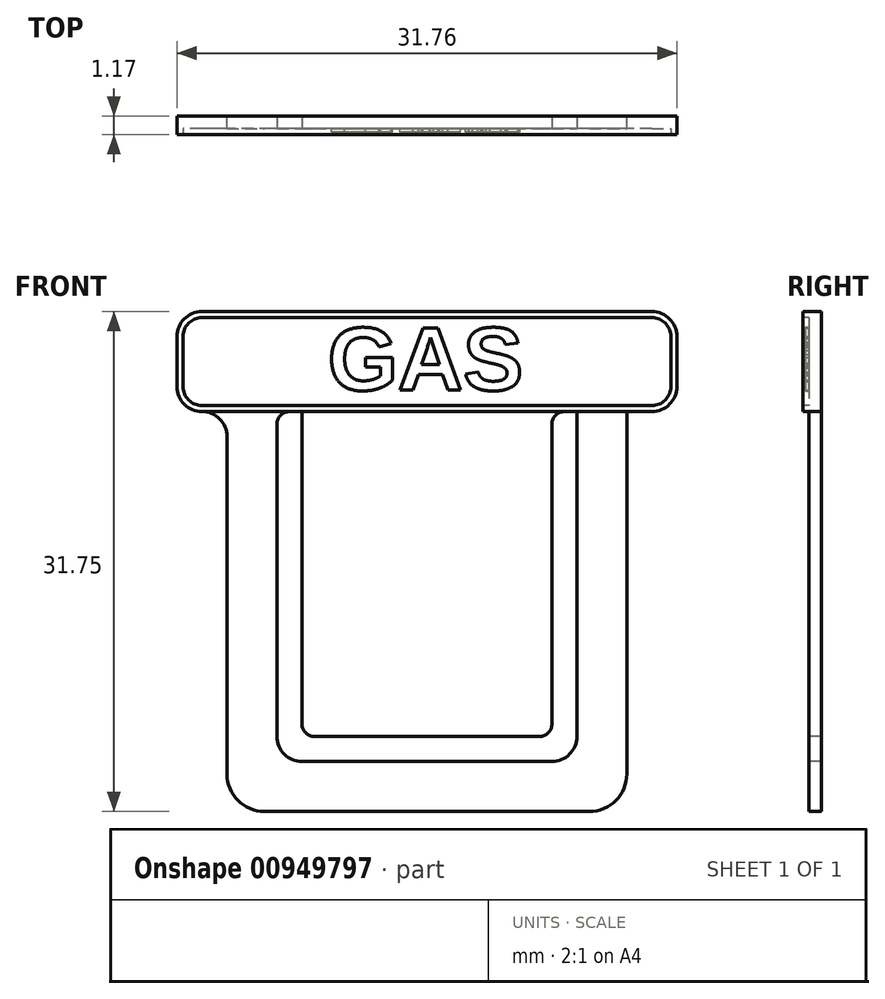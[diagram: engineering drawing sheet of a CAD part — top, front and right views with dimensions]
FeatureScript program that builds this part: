
annotation { "Feature Type Name" : "Feature", "Feature Type Description" : "" }
export const myFeature = defineFeature(function(context is Context, id is Id, definition is map)
    precondition{}
    {
        {
            var Q0;
            Q0=qCreatedBy(makeId("Front.planeOp"),FACE);
            var sketch = newSketch(context, id + "F0", { "sketchPlane" : qUnion([Q0])});
            skLineSegment(sketch, "E0.bottom", {"start": v(12.7, 12.7) * mm, "end": v(-12.7, 12.7) * mm});
            skLineSegment(sketch, "E0.top", {"start": v(12.7, -12.7) * mm, "end": v(-12.7, -12.7) * mm});
            skLineSegment(sketch, "E0.left", {"start": v(12.7, 12.7) * mm, "end": v(12.7, -12.7) * mm});
            skLineSegment(sketch, "E0.right", {"start": v(-12.7, 12.7) * mm, "end": v(-12.7, -12.7) * mm});
            skPoint(sketch, "E0.middle", {"position": v(0, 0) * mm});
            skSolve(sketch);
        }
        {
            var Q0;
            Q0=makeQuery(id+"F0.imprint","IMPRINT",FACE,{"disambiguationData":[TD([[makeQuery(id+"F0.imprint","IMPRINT",EDGE,{"derivedFrom":sQuery(id+"F0.wireOp",EDGE,"E0.bottom")}),1.0]])]});
            extrude(context, id + "F1", {"entities" : qUnion([Q0]), "depth" : 0.8 * mm, "offsetDistance" : 25.4 * mm});
        }
        {
            var Q0;
            Q0=makeQuery(id+"F1.opExtrude","SWEPT_EDGE",EDGE,{"disambiguationData":[OSD([sQuery(id+"F0.wireOp",EDGE,"E0.top"),sQuery(id+"F0.wireOp",EDGE,"E0.left")])]});
            var Q1;
            Q1=makeQuery(id+"F1.opExtrude","SWEPT_EDGE",EDGE,{"disambiguationData":[OSD([sQuery(id+"F0.wireOp",EDGE,"E0.top"),sQuery(id+"F0.wireOp",EDGE,"E0.right")])]});
            fillet(context, id + "F2", {"entities" : qUnion([Q0, Q1]), "radius" : 2.38 * mm, "tangentPropagation" : true, "allowEdgeOverflow" : false});
        }
        {
            var Q0;
            Q0=makeQuery(id+"F1.opExtrude","CAP_FACE",FACE,{"disambiguationData":[OSD([sQuery(id+"F0.wireOp",EDGE,"E0.bottom"),sQuery(id+"F0.wireOp",EDGE,"E0.top"),sQuery(id+"F0.wireOp",EDGE,"E0.left"),sQuery(id+"F0.wireOp",EDGE,"E0.right")])],"isStart":false});
            var sketch = newSketch(context, id + "F3", { "sketchPlane" : qUnion([Q0])});
            skLineSegment(sketch, "E1.bottom", {"start": v(9.52, 12.7) * mm, "end": v(-9.53, 12.7) * mm});
            skLineSegment(sketch, "E1.top", {"start": v(9.53, -9.53) * mm, "end": v(-9.52, -9.53) * mm});
            skLineSegment(sketch, "E1.left", {"start": v(9.52, 12.7) * mm, "end": v(9.53, -9.53) * mm});
            skLineSegment(sketch, "E1.right", {"start": v(-9.53, 12.7) * mm, "end": v(-9.52, -9.53) * mm});
            skPoint(sketch, "E1.middle", {"position": v(0, 0) * mm});
            skSolve(sketch);
        }
        {
            var Q0;
            Q0=makeQuery(id+"F3.imprint","IMPRINT",FACE,{"disambiguationData":[TD([[makeQuery(id+"F3.imprint","IMPRINT",EDGE,{"derivedFrom":sQuery(id+"F3.wireOp",EDGE,"E1.bottom")}),1.0]])]});
            extrude(context, id + "F4", {"entities" : qUnion([Q0]), "operationType" : NewBodyOperationType.REMOVE, "oppositeDirection" : true, "depth" : 4.93 * mm, "offsetDistance" : 25.4 * mm});
        }
        {
            var Q0;
            Q0=makeQuery(id+"F1.opExtrude","CAP_FACE",FACE,{"disambiguationData":[OSD([sQuery(id+"F0.wireOp",EDGE,"E0.bottom"),sQuery(id+"F0.wireOp",EDGE,"E0.top"),sQuery(id+"F0.wireOp",EDGE,"E0.left"),sQuery(id+"F0.wireOp",EDGE,"E0.right")])],"isStart":false});
            var sketch = newSketch(context, id + "F5", { "sketchPlane" : qUnion([Q0])});
            skLineSegment(sketch, "E2.bottom", {"start": v(-15.88, 12.7) * mm, "end": v(15.88, 12.7) * mm});
            skLineSegment(sketch, "E2.top", {"start": v(-15.88, 19.05) * mm, "end": v(15.88, 19.05) * mm});
            skLineSegment(sketch, "E2.left", {"start": v(-15.88, 12.7) * mm, "end": v(-15.88, 19.05) * mm});
            skLineSegment(sketch, "E2.right", {"start": v(15.87, 12.7) * mm, "end": v(15.87, 19.05) * mm});
            skSolve(sketch);
        }
        {
            var Q0;
            Q0=makeQuery(id+"F5.imprint","IMPRINT",FACE,{"disambiguationData":[TD([[makeQuery(id+"F5.imprint","IMPRINT",EDGE,{"derivedFrom":sQuery(id+"F5.wireOp",EDGE,"E2.top")}),-1.0]])]});
            extrude(context, id + "F6", {"entities" : qUnion([Q0]), "operationType" : NewBodyOperationType.ADD, "oppositeDirection" : true, "depth" : 0.8 * mm, "offsetDistance" : 25.4 * mm});
        }
        {
            var Q0;
            Q0=makeQuery(id+"F6.opExtrude","SWEPT_EDGE",EDGE,{"disambiguationData":[OSD([sQuery(id+"F5.wireOp",EDGE,"E2.top"),sQuery(id+"F5.wireOp",EDGE,"E2.left")])]});
            var Q1;
            Q1=makeQuery(id+"F6.opExtrude","SWEPT_EDGE",EDGE,{"disambiguationData":[OSD([sQuery(id+"F5.wireOp",EDGE,"E2.top"),sQuery(id+"F5.wireOp",EDGE,"E2.right")])]});
            var Q2;
            Q2=makeQuery(id+"F6.opExtrude","SWEPT_EDGE",EDGE,{"disambiguationData":[OSD([sQuery(id+"F5.wireOp",EDGE,"E2.bottom"),sQuery(id+"F5.wireOp",EDGE,"E2.right")])]});
            var Q3;
            Q3=makeQuery(id+"F1.opExtrude","SWEPT_EDGE",EDGE,{"disambiguationData":[OSD([sQuery(id+"F0.wireOp",EDGE,"E0.bottom"),sQuery(id+"F0.wireOp",EDGE,"E0.left")])]});
            var Q4;
            Q4=makeQuery(id+"F6.opExtrude","SWEPT_EDGE",EDGE,{"disambiguationData":[OSD([sQuery(id+"F5.wireOp",EDGE,"E2.bottom"),sQuery(id+"F5.wireOp",EDGE,"E2.left")])]});
            var Q5;
            Q5=makeQuery(id+"F1.opExtrude","SWEPT_EDGE",EDGE,{"disambiguationData":[OSD([sQuery(id+"F0.wireOp",EDGE,"E0.bottom"),sQuery(id+"F0.wireOp",EDGE,"E0.right")])]});
            fillet(context, id + "F7", {"entities" : qUnion([Q0, Q1, Q2, Q3, Q4, Q5]), "radius" : 1.59 * mm, "tangentPropagation" : true, "allowEdgeOverflow" : false});
        }
        {
            var Q0;
            Q0=makeQuery(id+"F4.boolean.opBoolean","COPY",EDGE,{"derivedFrom":makeQuery(id+"F4.opExtrude","SWEPT_EDGE",EDGE,{"disambiguationData":[OSD([sQuery(id+"F3.wireOp",EDGE,"E1.top"),sQuery(id+"F3.wireOp",EDGE,"E1.right")])]})});
            var Q1;
            Q1=makeQuery(id+"F4.boolean.opBoolean","COPY",EDGE,{"derivedFrom":makeQuery(id+"F4.opExtrude","SWEPT_EDGE",EDGE,{"disambiguationData":[OSD([sQuery(id+"F3.wireOp",EDGE,"E1.top"),sQuery(id+"F3.wireOp",EDGE,"E1.left")])]})});
            fillet(context, id + "F8", {"entities" : qUnion([Q0, Q1]), "radius" : 1.59 * mm, "tangentPropagation" : true, "allowEdgeOverflow" : false});
        }
        {
            var Q0;
            Q0=makeQuery(id+"F6.boolean.opBoolean","MERGE",FACE,{"derivedFrom":[makeQuery(id+"F1.opExtrude","CAP_FACE",FACE,{"disambiguationData":[OSD([sQuery(id+"F0.wireOp",EDGE,"E0.bottom"),sQuery(id+"F0.wireOp",EDGE,"E0.top"),sQuery(id+"F0.wireOp",EDGE,"E0.left"),sQuery(id+"F0.wireOp",EDGE,"E0.right")])],"isStart":false}),makeQuery(id+"F6.opExtrude","CAP_FACE",FACE,{"disambiguationData":[OSD([sQuery(id+"F5.wireOp",EDGE,"E2.bottom"),sQuery(id+"F5.wireOp",EDGE,"E2.top"),sQuery(id+"F5.wireOp",EDGE,"E2.left"),sQuery(id+"F5.wireOp",EDGE,"E2.right")])],"isStart":true})]});
            var sketch = newSketch(context, id + "F9", { "sketchPlane" : qUnion([Q0])});
            skLineSegment(sketch, "E3.bottom", {"start": v(-7.94, 12.7) * mm, "end": v(7.94, 12.7) * mm});
            skLineSegment(sketch, "E3.top", {"start": v(-7.94, -7.94) * mm, "end": v(7.94, -7.94) * mm});
            skLineSegment(sketch, "E3.left", {"start": v(-7.94, 12.7) * mm, "end": v(-7.94, -7.94) * mm});
            skLineSegment(sketch, "E3.right", {"start": v(7.94, 12.7) * mm, "end": v(7.94, -7.94) * mm});
            skSolve(sketch);
        }
        {
            var Q0;
            Q0=makeQuery(id+"F9.imprint","IMPRINT",FACE,{"disambiguationData":[TD([[makeQuery(id+"F9.imprint","IMPRINT",EDGE,{"derivedFrom":sQuery(id+"F9.wireOp",EDGE,"E3.bottom")}),1.0]])]});
            extrude(context, id + "F10", {"entities" : qUnion([Q0]), "operationType" : NewBodyOperationType.ADD, "oppositeDirection" : true, "depth" : 0.8 * mm, "offsetDistance" : 25.4 * mm});
        }
        {
            var Q0;
            Q0=makeQuery(id+"F10.opExtrude","SWEPT_EDGE",EDGE,{"disambiguationData":[OSD([sQuery(id+"F5.wireOp",EDGE,"E2.bottom"),sQuery(id+"F9.wireOp",EDGE,"E3.bottom"),sQuery(id+"F9.wireOp",EDGE,"E3.left")])]});
            var Q1;
            Q1=makeQuery(id+"F4.boolean.opBoolean","COPY",EDGE,{"derivedFrom":makeQuery(id+"F4.opExtrude","SWEPT_EDGE",EDGE,{"disambiguationData":[OSD([sQuery(id+"F0.wireOp",EDGE,"E0.bottom"),sQuery(id+"F3.wireOp",EDGE,"E1.bottom"),sQuery(id+"F3.wireOp",EDGE,"E1.right")])]})});
            var Q2;
            Q2=makeQuery(id+"F10.opExtrude","SWEPT_EDGE",EDGE,{"disambiguationData":[OSD([sQuery(id+"F5.wireOp",EDGE,"E2.bottom"),sQuery(id+"F9.wireOp",EDGE,"E3.bottom"),sQuery(id+"F9.wireOp",EDGE,"E3.right")])]});
            var Q3;
            Q3=makeQuery(id+"F4.boolean.opBoolean","COPY",EDGE,{"derivedFrom":makeQuery(id+"F4.opExtrude","SWEPT_EDGE",EDGE,{"disambiguationData":[OSD([sQuery(id+"F0.wireOp",EDGE,"E0.bottom"),sQuery(id+"F3.wireOp",EDGE,"E1.bottom"),sQuery(id+"F3.wireOp",EDGE,"E1.left")])]})});
            fillet(context, id + "F11", {"entities" : qUnion([Q0, Q1, Q2, Q3]), "radius" : 0.8 * mm, "tangentPropagation" : true, "allowEdgeOverflow" : false});
        }
        {
            var Q0;
            Q0=makeQuery(id+"F10.opExtrude","SWEPT_EDGE",EDGE,{"disambiguationData":[OSD([sQuery(id+"F9.wireOp",EDGE,"E3.top"),sQuery(id+"F9.wireOp",EDGE,"E3.left")])]});
            var Q1;
            Q1=makeQuery(id+"F10.opExtrude","SWEPT_EDGE",EDGE,{"disambiguationData":[OSD([sQuery(id+"F9.wireOp",EDGE,"E3.top"),sQuery(id+"F9.wireOp",EDGE,"E3.right")])]});
            fillet(context, id + "F12", {"entities" : qUnion([Q0, Q1]), "radius" : 0.8 * mm, "tangentPropagation" : true, "allowEdgeOverflow" : false});
        }
        {
            var Q0;
            Q0=makeQuery(id+"F10.boolean.opBoolean","MERGE",FACE,{"derivedFrom":[makeQuery(id+"F6.boolean.opBoolean","MERGE",FACE,{"derivedFrom":[makeQuery(id+"F1.opExtrude","CAP_FACE",FACE,{"disambiguationData":[OSD([sQuery(id+"F0.wireOp",EDGE,"E0.bottom"),sQuery(id+"F0.wireOp",EDGE,"E0.top"),sQuery(id+"F0.wireOp",EDGE,"E0.left"),sQuery(id+"F0.wireOp",EDGE,"E0.right")])],"isStart":false}),makeQuery(id+"F6.opExtrude","CAP_FACE",FACE,{"disambiguationData":[OSD([sQuery(id+"F5.wireOp",EDGE,"E2.bottom"),sQuery(id+"F5.wireOp",EDGE,"E2.top"),sQuery(id+"F5.wireOp",EDGE,"E2.left"),sQuery(id+"F5.wireOp",EDGE,"E2.right")])],"isStart":true})]}),makeQuery(id+"F10.opExtrude","CAP_FACE",FACE,{"disambiguationData":[OSD([sQuery(id+"F9.wireOp",EDGE,"E3.bottom"),sQuery(id+"F9.wireOp",EDGE,"E3.top"),sQuery(id+"F9.wireOp",EDGE,"E3.left"),sQuery(id+"F9.wireOp",EDGE,"E3.right")])],"isStart":true})]});
            var sketch = newSketch(context, id + "F13", { "sketchPlane" : qUnion([Q0])});
            skArc(sketch, "E4.0", {"start": v(-14.29, 19.05) * mm, "mid": v(-15.41, 18.59) * mm, "end": v(-15.88, 17.46) * mm});
            skLineSegment(sketch, "E5.0", {"start": v(-15.88, 14.29) * mm, "end": v(-15.88, 17.46) * mm});
            skArc(sketch, "E6.0", {"start": v(-15.88, 14.29) * mm, "mid": v(-15.41, 13.16) * mm, "end": v(-14.29, 12.7) * mm});
            skLineSegment(sketch, "E7.0", {"start": v(-14.29, 19.05) * mm, "end": v(14.29, 19.05) * mm});
            skArc(sketch, "E8.0", {"start": v(15.87, 17.46) * mm, "mid": v(15.41, 18.59) * mm, "end": v(14.29, 19.05) * mm});
            skLineSegment(sketch, "E9.0", {"start": v(15.87, 14.29) * mm, "end": v(15.87, 17.46) * mm});
            skArc(sketch, "E10.0", {"start": v(14.29, 12.7) * mm, "mid": v(15.41, 13.16) * mm, "end": v(15.87, 14.29) * mm});
            skLineSegment(sketch, "E11", {"start": v(-14.29, 12.7) * mm, "end": v(14.29, 12.7) * mm});
            skSolve(sketch);
        }
        {
            var Q0;
            Q0=makeQuery(id+"F13.imprint","IMPRINT",FACE,{"disambiguationData":[TD([[makeQuery(id+"F13.imprint","IMPRINT",EDGE,{"derivedFrom":sQuery(id+"F13.wireOp",EDGE,"E4.0")}),1.0]])]});
            extrude(context, id + "F14", {"entities" : qUnion([Q0]), "operationType" : NewBodyOperationType.ADD, "depth" : 0.38 * mm, "offsetDistance" : 25.4 * mm});
        }
        {
            var Q0;
            Q0=makeQuery(id+"F14.opExtrude","CAP_FACE",FACE,{"disambiguationData":[OSD([sQuery(id+"F13.wireOp",EDGE,"E4.0"),sQuery(id+"F13.wireOp",EDGE,"E5.0"),sQuery(id+"F13.wireOp",EDGE,"E6.0"),sQuery(id+"F13.wireOp",EDGE,"E7.0"),sQuery(id+"F13.wireOp",EDGE,"E8.0"),sQuery(id+"F13.wireOp",EDGE,"E9.0"),sQuery(id+"F13.wireOp",EDGE,"E10.0"),sQuery(id+"F13.wireOp",EDGE,"E11")])],"isStart":false});
            var sketch = newSketch(context, id + "F15", { "sketchPlane" : qUnion([Q0])});
            skArc(sketch, "E12.0", {"start": v(-14.29, 19.05) * mm, "mid": v(-15.41, 18.59) * mm, "end": v(-15.88, 17.46) * mm});
            skLineSegment(sketch, "E13.0", {"start": v(-14.29, 19.05) * mm, "end": v(14.29, 19.05) * mm});
            skLineSegment(sketch, "E14.0", {"start": v(-15.88, 14.29) * mm, "end": v(-15.88, 17.46) * mm});
            skArc(sketch, "E15.0", {"start": v(-15.88, 14.29) * mm, "mid": v(-15.41, 13.16) * mm, "end": v(-14.29, 12.7) * mm});
            skLineSegment(sketch, "E16.0", {"start": v(-14.29, 12.7) * mm, "end": v(14.29, 12.7) * mm});
            skArc(sketch, "E17.0", {"start": v(14.29, 12.7) * mm, "mid": v(15.41, 13.16) * mm, "end": v(15.87, 14.29) * mm});
            skArc(sketch, "E18.0", {"start": v(15.87, 17.46) * mm, "mid": v(15.41, 18.59) * mm, "end": v(14.29, 19.05) * mm});
            skArc(sketch, "E19", {"start": v(-14.29, 18.67) * mm, "mid": v(-15.14, 18.32) * mm, "end": v(-15.5, 17.46) * mm});
            skArc(sketch, "E20", {"start": v(-15.5, 14.29) * mm, "mid": v(-15.14, 13.43) * mm, "end": v(-14.29, 13.08) * mm});
            skArc(sketch, "E21", {"start": v(15.5, 17.46) * mm, "mid": v(15.14, 18.32) * mm, "end": v(14.29, 18.67) * mm});
            skArc(sketch, "E22", {"start": v(14.29, 13.08) * mm, "mid": v(15.14, 13.43) * mm, "end": v(15.5, 14.29) * mm});
            skLineSegment(sketch, "E23", {"start": v(-14.29, 19.05) * mm, "end": v(-14.29, 12.7) * mm, "construction": true});
            skLineSegment(sketch, "E24", {"start": v(-15.88, 17.46) * mm, "end": v(15.87, 17.46) * mm, "construction": true});
            skLineSegment(sketch, "E25", {"start": v(14.29, 19.05) * mm, "end": v(14.29, 12.7) * mm, "construction": true});
            skLineSegment(sketch, "E26", {"start": v(15.87, 14.29) * mm, "end": v(-15.88, 14.29) * mm, "construction": true});
            skLineSegment(sketch, "E27", {"start": v(14.29, 18.67) * mm, "end": v(-14.29, 18.67) * mm});
            skLineSegment(sketch, "E28", {"start": v(-15.5, 17.46) * mm, "end": v(-15.5, 14.29) * mm});
            skLineSegment(sketch, "E29", {"start": v(-14.29, 13.08) * mm, "end": v(14.29, 13.08) * mm});
            skLineSegment(sketch, "E30", {"start": v(15.5, 17.46) * mm, "end": v(15.5, 14.29) * mm});
            skSolve(sketch);
        }
        {
            var Q0;
            Q0=makeQuery(id+"F15.imprint","IMPRINT",FACE,{"disambiguationData":[TD([[makeQuery(id+"F15.imprint","IMPRINT",EDGE,{"derivedFrom":sQuery(id+"F15.wireOp",EDGE,"E19")}),1.0]])]});
            var Q1;
            {var subQ0=sQuery(id+"F9.wireOp",EDGE,"E3.right");var subQ1=sQuery(id+"F9.wireOp",EDGE,"E3.top");var subQ3=sQuery(id+"F0.wireOp",EDGE,"E0.bottom");var subQ4=sQuery(id+"F9.wireOp",EDGE,"E3.left");var subQ5=makeQuery(id+"F6.opExtrude","CAP_FACE",FACE,{"disambiguationData":[OSD([sQuery(id+"F5.wireOp",EDGE,"E2.bottom"),sQuery(id+"F5.wireOp",EDGE,"E2.top"),sQuery(id+"F5.wireOp",EDGE,"E2.left"),sQuery(id+"F5.wireOp",EDGE,"E2.right")])],"isStart":true});var subQ6=makeQuery(id+"F1.opExtrude","CAP_FACE",FACE,{"disambiguationData":[OSD([subQ3,sQuery(id+"F0.wireOp",EDGE,"E0.top"),sQuery(id+"F0.wireOp",EDGE,"E0.left"),sQuery(id+"F0.wireOp",EDGE,"E0.right")])],"isStart":false});var subQ7=makeQuery(id+"F10.opExtrude","CAP_FACE",FACE,{"disambiguationData":[OSD([sQuery(id+"F9.wireOp",EDGE,"E3.bottom"),subQ1,subQ4,subQ0])],"isStart":true});Q1=makeQuery(id+"F14.boolean.opBoolean","SPLIT",FACE,{"disambiguationData":[TD([makeQuery(id+"F10.opExtrude","SWEPT_FACE",FACE,{"disambiguationData":[OSD([subQ1])]})])],"derivedFrom":makeQuery(id+"F10.boolean.opBoolean","MERGE",FACE,{"derivedFrom":[makeQuery(id+"F6.boolean.opBoolean","MERGE",FACE,{"derivedFrom":[subQ6,subQ5]}),subQ7]})});}
            extrude(context, id + "F16", {"entities" : qUnion([Q0]), "operationType" : NewBodyOperationType.REMOVE, "endBound" : BoundingType.UP_TO_SURFACE, "oppositeDirection" : true, "depth" : 25.4 * mm, "endBoundEntityFace" : qUnion([Q1]), "offsetDistance" : 25.4 * mm});
        }
        {
            var Q0;
            Q0=qCreatedBy(makeId("Front.planeOp"),FACE);
            var sketch = newSketch(context, id + "F17", { "sketchPlane" : qUnion([Q0])});
            skText(sketch, "E31", { "text": "GAS", "fontName": "Arimo-Bold.ttf"});
            const initialGuessF17  = {"E31": [-0.00629, 0.01406, 1, 0, 0.00412]};
            skSetInitialGuess(sketch, initialGuessF17);
            skSolve(sketch);
        }
        {
            var Q0;
            Q0=qSketchRegion(id+"F17",true);
            extrude(context, id + "F18", {"entities" : qUnion([Q0]), "operationType" : NewBodyOperationType.ADD, "depth" : 1.02 * mm, "offsetDistance" : 25.4 * mm});
        }
    });
